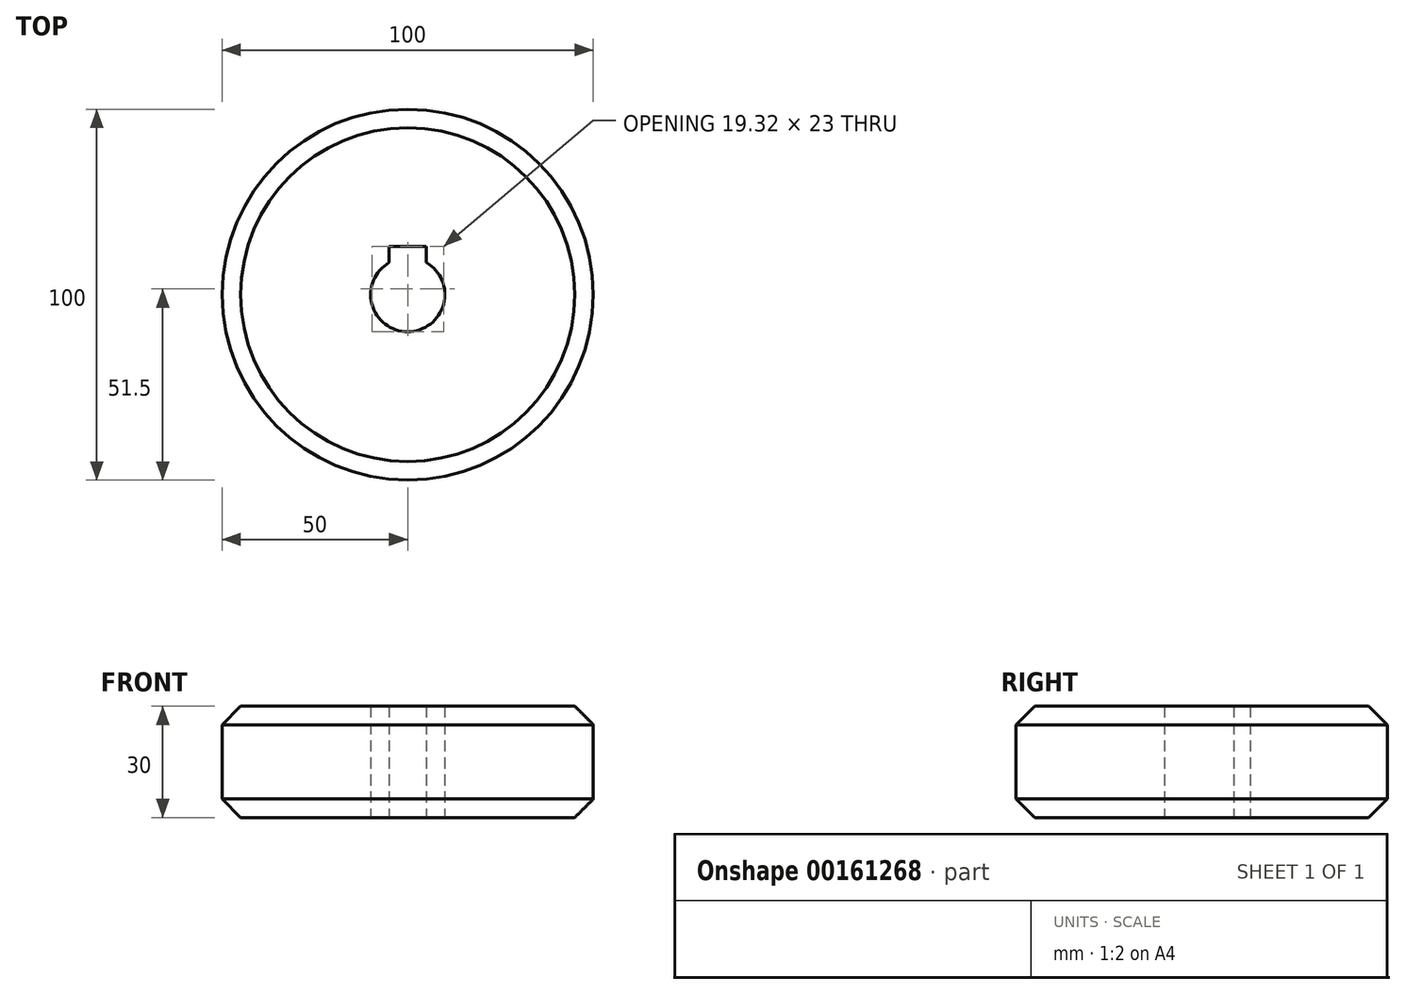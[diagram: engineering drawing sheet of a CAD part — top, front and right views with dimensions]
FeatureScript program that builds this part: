
annotation { "Feature Type Name" : "Feature", "Feature Type Description" : "" }
export const myFeature = defineFeature(function(context is Context, id is Id, definition is map)
    precondition{}
    {
        {
            var Q0;
            Q0=qCreatedBy(makeId("Top.planeOp"),FACE);
            var sketch = newSketch(context, id + "F0", { "sketchPlane" : qUnion([Q0])});
            skCircle(sketch, "E0", {"center": v(0, 0) * mm, "radius": 50 * mm});
            skArc(sketch, "E1", {"start": v(-5, 8.66) * mm, "mid": v(0, -10) * mm, "end": v(5, 8.66) * mm});
            skLineSegment(sketch, "E2", {"start": v(0, 64.75) * mm, "end": v(0, -58.31) * mm, "construction": true});
            skLineSegment(sketch, "E3", {"start": v(-5, 8.66) * mm, "end": v(-5, 13) * mm});
            skLineSegment(sketch, "E4", {"start": v(-5, 13) * mm, "end": v(0, 13) * mm});
            skLineSegment(sketch, "E5.MirrorCS", {"start": v(5, 13) * mm, "end": v(0, 13) * mm});
            skLineSegment(sketch, "E6.MirrorCS", {"start": v(5, 8.66) * mm, "end": v(5, 13) * mm});
            skSolve(sketch);
        }
        {
            var Q0;
            Q0=makeQuery(id+"F0.imprint","IMPRINT",FACE,{"disambiguationData":[TD([[makeQuery(id+"F0.imprint","IMPRINT",EDGE,{"derivedFrom":sQuery(id+"F0.wireOp",EDGE,"E0")}),1.0]])]});
            extrude(context, id + "F1", {"entities" : qUnion([Q0]), "depth" : 30 * mm});
        }
        {
            var Q0;
            Q0=makeQuery(id+"F1.opExtrude","CAP_EDGE",EDGE,{"disambiguationData":[OSD([sQuery(id+"F0.wireOp",EDGE,"E0")])],"isStart":false});
            var Q1;
            Q1=makeQuery(id+"F1.opExtrude","CAP_EDGE",EDGE,{"disambiguationData":[OSD([sQuery(id+"F0.wireOp",EDGE,"E0")])],"isStart":true});
            chamfer(context, id + "F2", {"entities" : qUnion([Q0, Q1]), "width" : 5 * mm, "tangentPropagation" : true});
        }
    });
